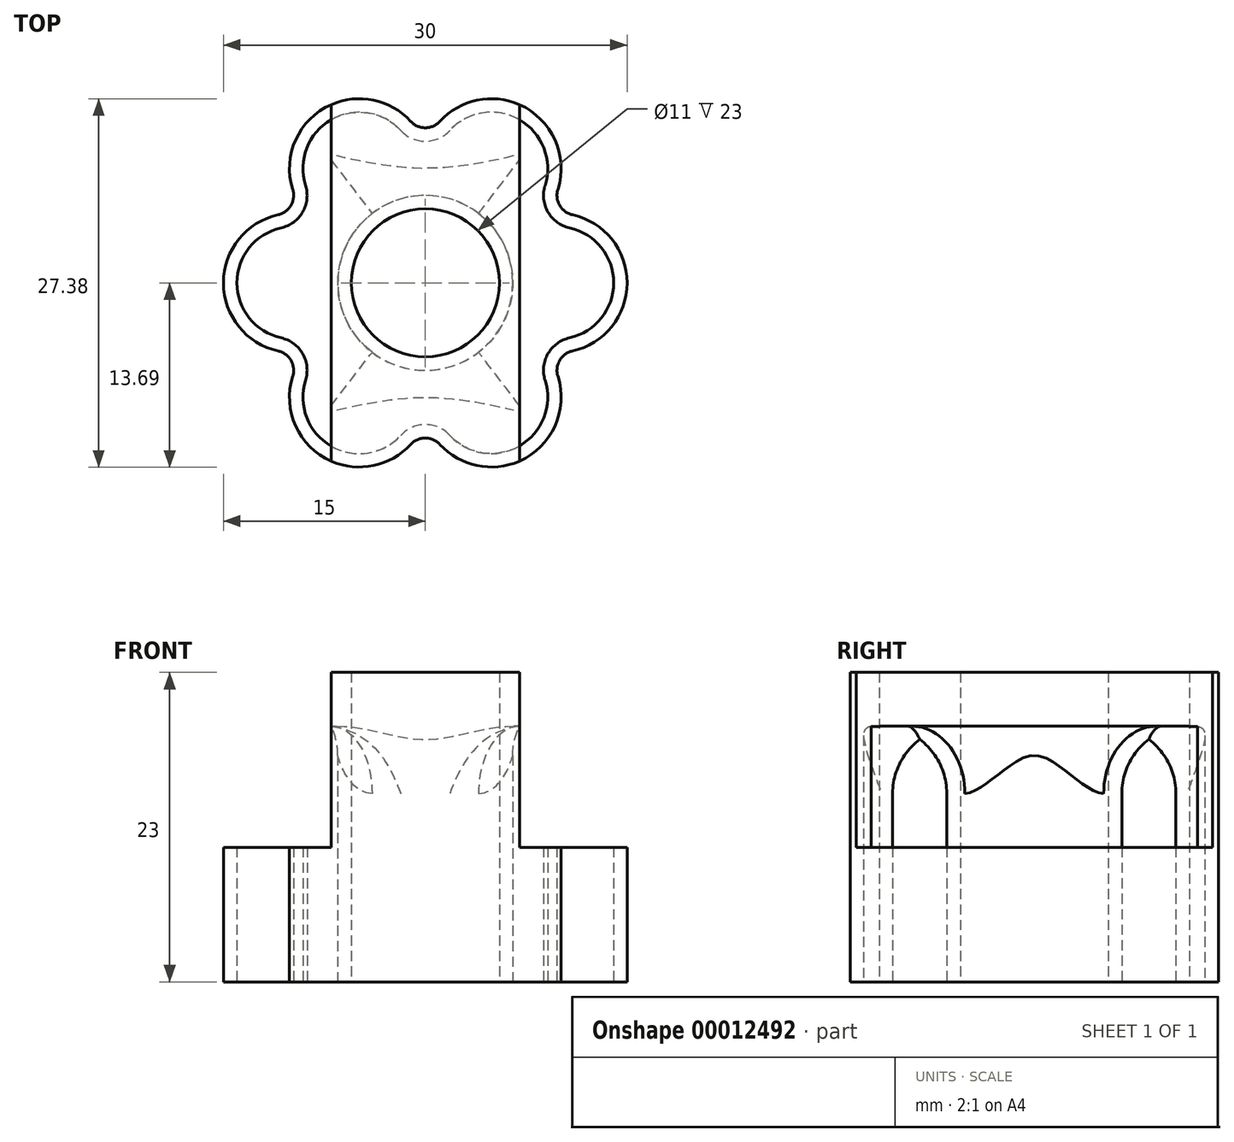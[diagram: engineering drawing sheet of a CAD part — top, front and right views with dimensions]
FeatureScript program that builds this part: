
annotation { "Feature Type Name" : "Feature", "Feature Type Description" : "" }
export const myFeature = defineFeature(function(context is Context, id is Id, definition is map)
    precondition{}
    {
        {
            var Q0;
            Q0=qCreatedBy(makeId("Top.planeOp"),FACE);
            var sketch = newSketch(context, id + "F0", { "sketchPlane" : qUnion([Q0])});
            skCircle(sketch, "E0.cCircle", {"center": v(0, 0) * mm, "radius": 8.5 * mm, "construction": true});
            skLineSegment(sketch, "E0.0", {"start": v(-4.9, 8.5) * mm, "end": v(4.9, 8.5) * mm, "construction": true});
            skLineSegment(sketch, "E0.1", {"start": v(4.9, 8.5) * mm, "end": v(9.81, 0) * mm, "construction": true});
            skLineSegment(sketch, "E0.2", {"start": v(9.81, 0) * mm, "end": v(4.9, -8.5) * mm, "construction": true});
            skLineSegment(sketch, "E0.3", {"start": v(4.9, -8.5) * mm, "end": v(-4.9, -8.5) * mm, "construction": true});
            skLineSegment(sketch, "E0.4", {"start": v(-4.9, -8.5) * mm, "end": v(-9.81, 0) * mm, "construction": true});
            skLineSegment(sketch, "E0.5", {"start": v(-9.81, 0) * mm, "end": v(-4.9, 8.5) * mm, "construction": true});
            skPoint(sketch, "E0.0.midPoint", {"position": v(0, 8.5) * mm});
            skCircle(sketch, "E1", {"center": v(0, 0) * mm, "radius": 15 * mm, "construction": true});
            skArc(sketch, "E2", {"start": v(-1.09, 12) * mm, "mid": v(-7.5, 13) * mm, "end": v(-9.85, 6.94) * mm});
            skArc(sketch, "E3", {"start": v(9.85, 6.94) * mm, "mid": v(7.5, 13) * mm, "end": v(1.09, 12) * mm});
            skArc(sketch, "E4", {"start": v(10.94, -5.06) * mm, "mid": v(15, 0) * mm, "end": v(10.94, 5.06) * mm});
            skArc(sketch, "E5", {"start": v(1.09, -12) * mm, "mid": v(7.5, -13) * mm, "end": v(9.85, -6.94) * mm});
            skArc(sketch, "E6", {"start": v(-9.85, -6.94) * mm, "mid": v(-7.5, -13) * mm, "end": v(-1.09, -12) * mm});
            skArc(sketch, "E7", {"start": v(-10.94, 5.06) * mm, "mid": v(-15, 0) * mm, "end": v(-10.94, -5.06) * mm});
            skCircle(sketch, "E8", {"center": v(0, 0) * mm, "radius": 13 * mm, "construction": true});
            skArc(sketch, "E9", {"start": v(-10.94, 5.06) * mm, "mid": v(-9.98, 5.76) * mm, "end": v(-9.85, 6.94) * mm});
            skArc(sketch, "E10", {"start": v(-1.09, 12) * mm, "mid": v(0, 11.53) * mm, "end": v(1.09, 12) * mm});
            skArc(sketch, "E11", {"start": v(9.85, 6.94) * mm, "mid": v(9.98, 5.76) * mm, "end": v(10.94, 5.06) * mm});
            skArc(sketch, "E12", {"start": v(10.94, -5.06) * mm, "mid": v(9.98, -5.76) * mm, "end": v(9.85, -6.94) * mm});
            skArc(sketch, "E13", {"start": v(1.09, -12) * mm, "mid": v(0, -11.53) * mm, "end": v(-1.09, -12) * mm});
            skArc(sketch, "E14", {"start": v(-9.85, -6.94) * mm, "mid": v(-9.98, -5.76) * mm, "end": v(-10.94, -5.06) * mm});
            skCircle(sketch, "E15", {"center": v(0, 0) * mm, "radius": 5.5 * mm});
            skLineSegment(sketch, "E16", {"start": v(0, 27.62) * mm, "end": v(0, -31.46) * mm, "construction": true});
            skSolve(sketch);
        }
        {
            var Q0;
            Q0=makeQuery(id+"F0.imprint","IMPRINT",FACE,{"disambiguationData":[TD([[makeQuery(id+"F0.imprint","IMPRINT",EDGE,{"derivedFrom":sQuery(id+"F0.wireOp",EDGE,"E2")}),1.0]])]});
            extrude(context, id + "F1", {"entities" : qUnion([Q0]), "depth" : 20 * mm});
        }
        {
            var Q0;
            Q0=makeQuery(id+"F1.opExtrude","CAP_FACE",FACE,{"disambiguationData":[OSD([sQuery(id+"F0.wireOp",EDGE,"E2"),sQuery(id+"F0.wireOp",EDGE,"E3"),sQuery(id+"F0.wireOp",EDGE,"E4"),sQuery(id+"F0.wireOp",EDGE,"E5"),sQuery(id+"F0.wireOp",EDGE,"E6"),sQuery(id+"F0.wireOp",EDGE,"E7"),sQuery(id+"F0.wireOp",EDGE,"E9"),sQuery(id+"F0.wireOp",EDGE,"E10"),sQuery(id+"F0.wireOp",EDGE,"E11"),sQuery(id+"F0.wireOp",EDGE,"E12"),sQuery(id+"F0.wireOp",EDGE,"E13"),sQuery(id+"F0.wireOp",EDGE,"E14"),sQuery(id+"F0.wireOp",EDGE,"E15")])],"isStart":true});
            shell(context, id + "F2", {"entities" : qUnion([Q0]), "thickness" : 1 * mm});
        }
        {
            var Q0;
            Q0=qCreatedBy(makeId("Front.planeOp"),FACE);
            var sketch = newSketch(context, id + "F3", { "sketchPlane" : qUnion([Q0])});
            skLineSegment(sketch, "E17", {"start": v(-26.06, 10) * mm, "end": v(-7, 10) * mm});
            skLineSegment(sketch, "E18", {"start": v(-7, 10) * mm, "end": v(-7, 35) * mm});
            skLineSegment(sketch, "E19", {"start": v(-7, 35) * mm, "end": v(7, 35) * mm});
            skLineSegment(sketch, "E20", {"start": v(7, 35) * mm, "end": v(7, 10) * mm});
            skLineSegment(sketch, "E21", {"start": v(7, 10) * mm, "end": v(23.94, 10) * mm});
            skLineSegment(sketch, "E22", {"start": v(23.94, 10) * mm, "end": v(23.94, 40) * mm});
            skLineSegment(sketch, "E23", {"start": v(23.94, 40) * mm, "end": v(-26.06, 40) * mm});
            skLineSegment(sketch, "E24", {"start": v(-26.06, 40) * mm, "end": v(-26.06, 10) * mm});
            skSolve(sketch);
        }
        {
            var Q0;
            Q0=makeQuery(id+"F3.imprint","IMPRINT",FACE,{"disambiguationData":[TD([[makeQuery(id+"F3.imprint","IMPRINT",EDGE,{"derivedFrom":sQuery(id+"F3.wireOp",EDGE,"E17")}),1.0]])]});
            extrude(context, id + "F4", {"entities" : qUnion([Q0]), "operationType" : NewBodyOperationType.REMOVE, "endBound" : BoundingType.SYMMETRIC, "oppositeDirection" : true, "depth" : 30 * mm});
        }
        {
            var Q0;
            Q0=makeQuery(id+"F1.opExtrude","CAP_FACE",FACE,{"disambiguationData":[OSD([sQuery(id+"F0.wireOp",EDGE,"E2"),sQuery(id+"F0.wireOp",EDGE,"E3"),sQuery(id+"F0.wireOp",EDGE,"E4"),sQuery(id+"F0.wireOp",EDGE,"E5"),sQuery(id+"F0.wireOp",EDGE,"E6"),sQuery(id+"F0.wireOp",EDGE,"E7"),sQuery(id+"F0.wireOp",EDGE,"E9"),sQuery(id+"F0.wireOp",EDGE,"E10"),sQuery(id+"F0.wireOp",EDGE,"E11"),sQuery(id+"F0.wireOp",EDGE,"E12"),sQuery(id+"F0.wireOp",EDGE,"E13"),sQuery(id+"F0.wireOp",EDGE,"E14"),sQuery(id+"F0.wireOp",EDGE,"E15")])],"isStart":false});
            extrude(context, id + "F5", {"entities" : qUnion([Q0]), "operationType" : NewBodyOperationType.ADD, "depth" : 3 * mm});
        }
        {
            var Q0;
            {var subQ0=sQuery(id+"F0.wireOp",EDGE,"E3");Q0=makeQuery(id+"F2.opShell","OFFSET_EDGE",EDGE,{"disambiguationData":[OSD([subQ0]),TDD([makeQuery(id+"F1.opExtrude","CAP_EDGE",EDGE,{"disambiguationData":[OSD([subQ0])],"isStart":false})])]});}
            var Q1;
            {var subQ0=sQuery(id+"F0.wireOp",EDGE,"E5");Q1=makeQuery(id+"F2.opShell","OFFSET_EDGE",EDGE,{"disambiguationData":[OSD([subQ0]),TDD([makeQuery(id+"F1.opExtrude","CAP_EDGE",EDGE,{"disambiguationData":[OSD([subQ0])],"isStart":false})])]});}
            var Q2;
            {var subQ0=sQuery(id+"F0.wireOp",EDGE,"E15");Q2=makeQuery(id+"F2.opShell","OFFSET_EDGE",EDGE,{"disambiguationData":[OSD([subQ0]),TDD([makeQuery(id+"F1.opExtrude","CAP_EDGE",EDGE,{"disambiguationData":[OSD([subQ0])],"isStart":false})])]});}
            fillet(context, id + "F6", {"entities" : qUnion([Q0, Q1, Q2]), "radius" : 5 * mm, "tangentPropagation" : true, "allowEdgeOverflow" : false});
        }
    });
